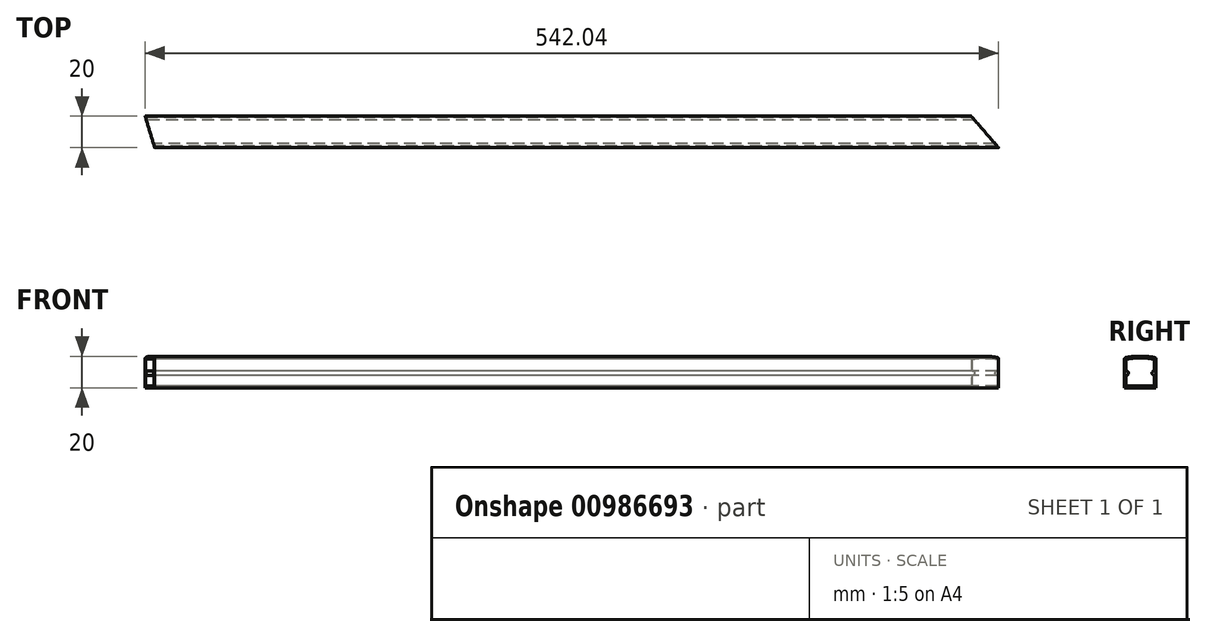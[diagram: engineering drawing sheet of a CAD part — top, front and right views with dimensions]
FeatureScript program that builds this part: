
annotation { "Feature Type Name" : "Feature", "Feature Type Description" : "" }
export const myFeature = defineFeature(function(context is Context, id is Id, definition is map)
    precondition{}
    {
        {
            var Q0;
            Q0=qCreatedBy(makeId("Right.planeOp"),FACE);
            var sketch = newSketch(context, id + "F0", { "sketchPlane" : qUnion([Q0])});
            skLineSegment(sketch, "E0.bottom", {"start": v(-10, -10) * mm, "end": v(10, -10) * mm});
            skLineSegment(sketch, "E0.top", {"start": v(-10, 10) * mm, "end": v(10, 10) * mm});
            skLineSegment(sketch, "E0.left", {"start": v(-10, -10) * mm, "end": v(-10, 10) * mm});
            skLineSegment(sketch, "E0.right", {"start": v(10, -10) * mm, "end": v(10, 10) * mm});
            skPoint(sketch, "E0.middle", {"position": v(0, 0) * mm});
            skSolve(sketch);
        }
        {
            var Q0;
            Q0=qCreatedBy(makeId("Right.planeOp"),FACE);
            var sketch = newSketch(context, id + "F1", { "sketchPlane" : qUnion([Q0])});
            skLineSegment(sketch, "E1.0", {"start": v(0, -10) * mm, "end": v(10, -10) * mm});
            skLineSegment(sketch, "E1.3", {"start": v(10, -10) * mm, "end": v(10, -0.2) * mm});
            skPoint(sketch, "E1.4", {"position": v(0, 0) * mm});
            skLineSegment(sketch, "E2.0", {"start": v(9, -9) * mm, "end": v(9, -2.2) * mm});
            skLineSegment(sketch, "E2.1", {"start": v(0, -9) * mm, "end": v(9, -9) * mm});
            skLineSegment(sketch, "E3", {"start": v(10, -0.2) * mm, "end": v(9, -0.2) * mm});
            skArc(sketch, "E4", {"start": v(9, -0.2) * mm, "mid": v(8.5, -0.7) * mm, "end": v(9, -1.2) * mm});
            skArc(sketch, "E5", {"start": v(9, -2.2) * mm, "mid": v(9.5, -1.7) * mm, "end": v(9, -1.2) * mm});
            skLineSegment(sketch, "E6", {"start": v(0, -9) * mm, "end": v(0, -10) * mm});
            skPoint(sketch, "E1.1.end.orphan", {"position": v(10, 10) * mm});
            skPoint(sketch, "E1.1.start.orphan", {"position": v(-10, 10) * mm});
            skPoint(sketch, "E1.2.end.orphan", {"position": v(-10, 10) * mm});
            skPoint(sketch, "E1.2.start.orphan", {"position": v(-10, -10) * mm});
            skPoint(sketch, "E7.orphan", {"position": v(-9, -9) * mm});
            skSolve(sketch);
        }
        {
            var Q0;
            Q0=qSketchRegion(id+"F1",true);
            extrude(context, id + "F2", {"entities" : qUnion([Q0]), "depth" : 1000 * mm, "offsetDistance" : 25 * mm});
        }
        {
            var Q0;
            Q0=qCreatedBy(makeId("Right.planeOp"),FACE);
            var sketch = newSketch(context, id + "F3", { "sketchPlane" : qUnion([Q0])});
            skPoint(sketch, "E8.2", {"position": v(0, 0) * mm});
            skLineSegment(sketch, "E8.5", {"start": v(10, -0.2) * mm, "end": v(9, -0.2) * mm});
            skArc(sketch, "E8.6", {"start": v(9, -0.2) * mm, "mid": v(8.5, -0.7) * mm, "end": v(9, -1.2) * mm});
            skArc(sketch, "E8.7", {"start": v(9, -2.2) * mm, "mid": v(9.5, -1.7) * mm, "end": v(9, -1.2) * mm});
            skPoint(sketch, "E8.9", {"position": v(10, 10) * mm});
            skPoint(sketch, "E8.10", {"position": v(10, 10) * mm});
            skPoint(sketch, "E8.11", {"position": v(-10, 10) * mm});
            skPoint(sketch, "E8.12", {"position": v(-10, 10) * mm});
            skPoint(sketch, "E8.13", {"position": v(-10, -10) * mm});
            skPoint(sketch, "E8.14", {"position": v(-9, -9) * mm});
            skPoint(sketch, "E8.15", {"position": v(-10, -10) * mm});
            skPoint(sketch, "E8.1.end.orphan", {"position": v(10, -0.2) * mm});
            skPoint(sketch, "E8.1.start.orphan", {"position": v(10, -10) * mm});
            skPoint(sketch, "E8.3.end.orphan", {"position": v(9, -2.2) * mm});
            skPoint(sketch, "E8.3.start.orphan", {"position": v(9, -9) * mm});
            skPoint(sketch, "E8.4.end.orphan", {"position": v(9, -9) * mm});
            skPoint(sketch, "E8.4.start.orphan", {"position": v(0, -9) * mm});
            skPoint(sketch, "E8.0.end.orphan", {"position": v(10, -10) * mm});
            skPoint(sketch, "E8.0.start.orphan", {"position": v(0, -10) * mm});
            skPoint(sketch, "E8.8.end.orphan", {"position": v(0, -10) * mm});
            skPoint(sketch, "E8.8.start.orphan", {"position": v(0, -9) * mm});
            skLineSegment(sketch, "E9", {"start": v(10, -0.2) * mm, "end": v(10, 8.17) * mm});
            skArc(sketch, "E10", {"start": v(9.18, 9.15) * mm, "mid": v(4.61, 9.79) * mm, "end": v(0, 10) * mm});
            skLineSegment(sketch, "E11", {"start": v(0, 10) * mm, "end": v(-15.57, 10) * mm, "construction": true});
            skPoint(sketch, "E12.visualSharp", {"position": v(10, 8.99) * mm});
            skArc(sketch, "E12.filletArc", {"start": v(10, 8.17) * mm, "mid": v(9.77, 8.8) * mm, "end": v(9.18, 9.15) * mm});
            skArc(sketch, "E13.0", {"start": v(9, 8.17) * mm, "mid": v(4.52, 8.8) * mm, "end": v(0, 9) * mm});
            skLineSegment(sketch, "E13.1", {"start": v(9, 0.8) * mm, "end": v(9, 8.17) * mm});
            skArc(sketch, "E13.2", {"start": v(9, 0.8) * mm, "mid": v(7.5, -0.7) * mm, "end": v(9, -2.2) * mm});
            skLineSegment(sketch, "E14", {"start": v(0, 10) * mm, "end": v(0, 9) * mm});
            skSolve(sketch);
        }
        {
            var Q0;
            Q0=qSketchRegion(id+"F3",true);
            extrude(context, id + "F4", {"entities" : qUnion([Q0]), "depth" : 1000 * mm, "offsetDistance" : 25 * mm});
        }
        {
            var Q0;
            Q0=makeQuery(id+"F2.opExtrude","SWEPT_BODY",BODY,{"disambiguationData":[OSD([sQuery(id+"F1.wireOp",EDGE,"E1.0"),sQuery(id+"F1.wireOp",EDGE,"E1.3"),sQuery(id+"F1.wireOp",EDGE,"E2.0"),sQuery(id+"F1.wireOp",EDGE,"E2.1"),sQuery(id+"F1.wireOp",EDGE,"E3"),sQuery(id+"F1.wireOp",EDGE,"E4"),sQuery(id+"F1.wireOp",EDGE,"E5"),sQuery(id+"F1.wireOp",EDGE,"E6")])]});
            var Q1;
            Q1=qCreatedBy(makeId("Front.planeOp"),FACE);
            mirror(context, id + "F5", {"operationType" : NewBodyOperationType.ADD, "entities" : qUnion([Q0]), "mirrorPlane" : qUnion([Q1])});
        }
        {
            var Q0;
            Q0=makeQuery(id+"F4.opExtrude","SWEPT_BODY",BODY,{"disambiguationData":[OSD([sQuery(id+"F3.wireOp",EDGE,"E8.5"),sQuery(id+"F3.wireOp",EDGE,"E8.6"),sQuery(id+"F3.wireOp",EDGE,"E8.7"),sQuery(id+"F3.wireOp",EDGE,"E9"),sQuery(id+"F3.wireOp",EDGE,"E10"),sQuery(id+"F3.wireOp",EDGE,"E12.filletArc"),sQuery(id+"F3.wireOp",EDGE,"E13.0"),sQuery(id+"F3.wireOp",EDGE,"E13.1"),sQuery(id+"F3.wireOp",EDGE,"E13.2"),sQuery(id+"F3.wireOp",EDGE,"E14")])]});
            var Q1;
            Q1=qCreatedBy(makeId("Front.planeOp"),FACE);
            mirror(context, id + "F6", {"operationType" : NewBodyOperationType.ADD, "entities" : qUnion([Q0]), "mirrorPlane" : qUnion([Q1])});
        }
        {
            var Q0;
            Q0=qCreatedBy(makeId("Top.planeOp"),FACE);
            var sketch = newSketch(context, id + "F7", { "sketchPlane" : qUnion([Q0])});
            skLineSegment(sketch, "E15", {"start": v(0, 0) * mm, "end": v(0, -10) * mm});
            skLineSegment(sketch, "E16", {"start": v(0, 10) * mm, "end": v(0, 0) * mm});
            skLineSegment(sketch, "E17", {"start": v(524.65, 10) * mm, "end": v(542.04, -10) * mm});
            skLineSegment(sketch, "E18", {"start": v(524.65, 10) * mm, "end": v(709.91, 10) * mm});
            skLineSegment(sketch, "E19.bottom", {"start": v(542.04, -10) * mm, "end": v(1016.96, -10) * mm});
            skLineSegment(sketch, "E19.top", {"start": v(524.65, 10) * mm, "end": v(1016.96, 10) * mm});
            skLineSegment(sketch, "E19.right", {"start": v(1016.96, -10) * mm, "end": v(1016.96, 10) * mm});
            skLineSegment(sketch, "E20", {"start": v(542.04, 10) * mm, "end": v(542.04, -10) * mm, "construction": true});
            skLineSegment(sketch, "E21", {"start": v(0, 10) * mm, "end": v(6.04, -10) * mm});
            skLineSegment(sketch, "E22", {"start": v(0, -10) * mm, "end": v(6.04, -10) * mm});
            skSolve(sketch);
        }
        {
            var Q0;
            Q0=qSketchRegion(id+"F7",true);
            extrude(context, id + "F8", {"entities" : qUnion([Q0]), "operationType" : NewBodyOperationType.REMOVE, "endBound" : BoundingType.THROUGH_ALL, "depth" : 25 * mm, "offsetDistance" : 25 * mm, "hasSecondDirection" : true, "secondDirectionBound" : SecondDirectionBoundingType.THROUGH_ALL, "secondDirectionOppositeDirection" : true, "secondDirectionDepth" : 25 * mm});
        }
    });
